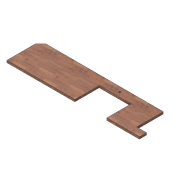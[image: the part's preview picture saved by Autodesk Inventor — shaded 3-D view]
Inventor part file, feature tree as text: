
AUTODESK INVENTOR PART (.ipt)
format: ipt  version: 2018 (Build 220112000, 112)  size: 148,480 bytes
history: native  units: mm
features: extrude x3, sketch x3, chamfer x2, projected_geometry x2, hole x1
ambient origin geometry x8: Origin, YZ Plane, XZ Plane, XY Plane, X Axis, Y Axis, Z Axis, Center Point
bodies: Solid1 (feature_tree)
feature tree (11):
  extrude  "Extrusion1"  Depth=38.0mm TaperAngle=0.0deg
  extrude  "Extrusion3"  Depth=2492.0mm
  chamfer  "Chamfer1"  Distance=500.0mm
  extrude  "Extrusion2"  Depth=10.0mm TaperAngle=0.0deg
  chamfer  "Chamfer2"  Distance=100.0mm Angle=45.0deg
  hole  "Hole1"  [1 undecoded]
  sketch  "Sketch2"  dims[d2=635.0mm d5=38.0mm d6=0.0mm]
  projected_geometry  "Projected Loop1"
  sketch  "Sketch3"  dims[d7=5.0mm d8=2.0mm d9=45.0deg d10=2492.0mm]
  projected_geometry  "Projected Loop2"
  sketch  "Sketch4"  dims[d11=185.0mm d12=500.0mm d13=10.0mm d14=0.0mm d15=100.0mm d16=2.0mm d17=45.0deg d18=600.0mm d19=460.0mm d20=615.0mm d21=10.0mm d22=0.0mm d23=35.0mm d24=6.0mm d25=4.0mm d26=2.0mm d27=90.0deg d28=8.0mm d29=20.594885mm]
note: 1 required parameter value undecoded (feature->parameter linkage not recoverable at this tier; creation-order binding heuristic only, values carry confidence <= 0.55)
